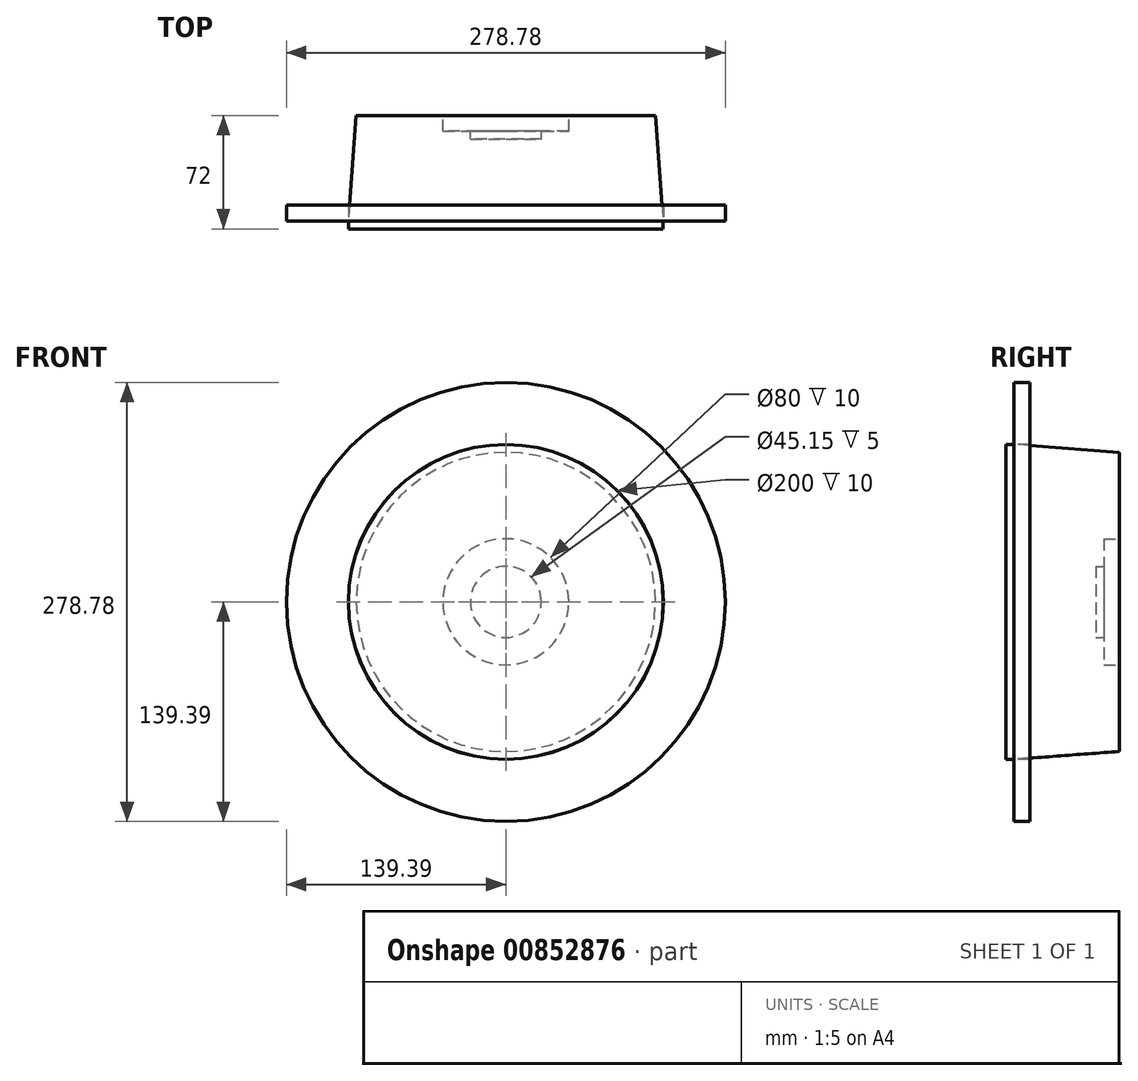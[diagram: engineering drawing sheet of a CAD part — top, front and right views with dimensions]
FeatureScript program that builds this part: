
annotation { "Feature Type Name" : "Feature", "Feature Type Description" : "" }
export const myFeature = defineFeature(function(context is Context, id is Id, definition is map)
    precondition{}
    {
        {
            var Q0;
            Q0=qCreatedBy(makeId("Front.planeOp"),FACE);
            var sketch = newSketch(context, id + "F0", { "sketchPlane" : qUnion([Q0])});
            skCircle(sketch, "E0", {"center": v(0, 0) * mm, "radius": 100 * mm});
            skLineSegment(sketch, "E1.bottom", {"start": v(90.04, 43.5) * mm, "end": v(90.04, 43.5) * mm});
            skLineSegment(sketch, "E1.top", {"start": v(90.04, -43.5) * mm, "end": v(90.04, -43.5) * mm});
            skCircle(sketch, "E2", {"center": v(0, 0) * mm, "radius": 139.39 * mm});
            skCircle(sketch, "E3", {"center": v(0, 0) * mm, "radius": 99.95 * mm});
            skSolve(sketch);
        }
        {
            var Q0;
            Q0=makeQuery(id+"F0.imprint","IMPRINT",FACE,{"disambiguationData":[TD([[makeQuery(id+"F0.imprint","IMPRINT",EDGE,{"derivedFrom":sQuery(id+"F0.wireOp",EDGE,"E2")}),1.0]])]});
            extrude(context, id + "F1", {"entities" : qUnion([Q0]), "oppositeDirection" : true, "depth" : 10 * mm, "offsetDistance" : 25 * mm});
        }
        {
            var Q0;
            {var subQ1=sQuery(id+"F0.wireOp",EDGE,"O6Og0VBV-7w1m-iwyO-GZB4-oZ87gUU7icq7");Q0=makeQuery(id+"F0.imprint","IMPRINT",FACE,{"disambiguationData":[TD([[makeQuery(id+"F0.imprint","IMPRINT",EDGE,{"derivedFrom":subQ1}),-1.0]])]});}
            var Q1;
            {var subQ0=sQuery(id+"F0.wireOp",EDGE,"E1.right");Q1=makeQuery(id+"F0.imprint","IMPRINT",FACE,{"disambiguationData":[TD([[makeQuery(id+"F0.imprint","IMPRINT",EDGE,{"derivedFrom":subQ0}),1.0]])]});}
            var Q2;
            Q2=makeQuery(id+"F0.imprint","IMPRINT",FACE,{"disambiguationData":[TD([[makeQuery(id+"F0.imprint","IMPRINT",EDGE,{"derivedFrom":sQuery(id+"F0.wireOp",EDGE,"O6Og0VBV-7w1m-iwyO-GZB4-oZ87gUU7icq7")}),1.0]])]});
            var Q3;
            Q3=makeQuery(id+"F0.imprint","IMPRINT",FACE,{"disambiguationData":[TD([[makeQuery(id+"F0.imprint","IMPRINT",EDGE,{"derivedFrom":sQuery(id+"F0.wireOp",EDGE,"GIwreYSu-AWBa-Gf9F-D9ee-HEHceEFpZMHu")}),-1.0]])]});
            var Q4;
            Q4=makeQuery(id+"F0.imprint","IMPRINT",FACE,{"disambiguationData":[TD([[makeQuery(id+"F0.imprint","IMPRINT",EDGE,{"derivedFrom":sQuery(id+"F0.wireOp",EDGE,"E2")}),1.0]])]});
            var Q5;
            {var subQ0=sQuery(id+"F0.wireOp",EDGE,"iStEkPqN-RXga-rDrQ-Osgs-Vn1kGgOUYUa5");Q5=makeQuery(id+"F0.imprint","IMPRINT",FACE,{"disambiguationData":[TD([[makeQuery(id+"F0.imprint","IMPRINT",EDGE,{"derivedFrom":subQ0}),-1.0]])]});}
            extrude(context, id + "F2", {"entities" : qUnion([Q0, Q1, Q2, Q3, Q4, Q5]), "oppositeDirection" : true, "depth" : 10 * mm, "offsetDistance" : 25 * mm});
        }
        {
            var Q0;
            {var subQ0=sQuery(id+"F0.wireOp",EDGE,"E3");Q0=makeQuery(id+"F3zxJdrnI9NYqlr_0.boolean.opBoolean","MERGE",FACE,{"derivedFrom":[makeQuery(id+"F2.opExtrude","CAP_FACE",FACE,{"disambiguationData":[OSD([sQuery(id+"F0.wireOp",EDGE,"E0"),sQuery(id+"F0.wireOp",EDGE,"E1.right"),sQuery(id+"F0.wireOp",EDGE,"GIwreYSu-AWBa-Gf9F-D9ee-HEHceEFpZMHu"),sQuery(id+"F0.wireOp",EDGE,"1ppw7uot-TYSR-niU3-FFL4-BmLDpTlKCJTZ"),sQuery(id+"F0.wireOp",EDGE,"iStEkPqN-RXga-rDrQ-Osgs-Vn1kGgOUYUa5"),sQuery(id+"F0.wireOp",EDGE,"E2"),subQ0])],"isStart":true}),makeQuery(id+"F3zxJdrnI9NYqlr_0.opExtrude","CAP_FACE",FACE,{"disambiguationData":[OSD([subQ0])],"isStart":true})]});}
            var sketch = newSketch(context, id + "F3", { "sketchPlane" : qUnion([Q0])});
            skCircle(sketch, "E4", {"center": v(0, 0) * mm, "radius": 100 * mm});
            skSolve(sketch);
        }
        {
            var Q0;
            Q0=makeQuery(id+"F0.imprint","IMPRINT",FACE,{"disambiguationData":[TD([[makeQuery(id+"F0.imprint","IMPRINT",EDGE,{"derivedFrom":sQuery(id+"F0.wireOp",EDGE,"E3")}),1.0]])]});
            extrude(context, id + "F4", {"entities" : qUnion([Q0]), "depth" : 5 * mm, "offsetDistance" : 25 * mm});
        }
        {
            var Q0;
            Q0=makeQuery(id+"F1.opExtrude","CAP_FACE",FACE,{"disambiguationData":[OSD([sQuery(id+"F0.wireOp",EDGE,"E0"),sQuery(id+"F0.wireOp",EDGE,"E2")])],"isStart":false});
            cPlane(context, id + "F5", {"entities" : qUnion([Q0]), "cplaneType" : CPlaneType.OFFSET, "offset" : 57 * mm, "width" : 150 * mm, "height" : 150 * mm});
        }
        {
            var Q0;
            Q0=qCreatedBy(id+"F5.planeOp",FACE);
            var sketch = newSketch(context, id + "F6", { "sketchPlane" : qUnion([Q0])});
            skCircle(sketch, "E5", {"center": v(0, 0) * mm, "radius": 95 * mm});
            skSolve(sketch);
        }
        {
            var Q1;
            Q1 = qSketchRegion(id + "F3", true);
            var Q2;
            Q2 = qSketchRegion(id + "F6", true);
            loft(context, id + "F7", {"operationType" : NewBodyOperationType.ADD, "sheetProfilesArray" : [{ "sheetProfileEntities" : qUnion([Q1]) }, { "sheetProfileEntities" : qUnion([Q2]) }]});
        }
        {
            var Q0;
            Q0=qCreatedBy(id+"F5.planeOp",FACE);
            var sketch = newSketch(context, id + "F8", { "sketchPlane" : qUnion([Q0])});
            skCircle(sketch, "E6", {"center": v(0, 0) * mm, "radius": 40 * mm});
            skSolve(sketch);
        }
        {
            var Q0;
            Q0 = qSketchRegion(id + "F8", true);
            extrude(context, id + "F9", {"entities" : qUnion([Q0]), "operationType" : NewBodyOperationType.REMOVE, "oppositeDirection" : true, "depth" : 10 * mm, "offsetDistance" : 25 * mm});
        }
        {
            var Q0;
            Q0=makeQuery(id+"F9.boolean.opBoolean","COPY",FACE,{"derivedFrom":makeQuery(id+"F9.opExtrude","CAP_FACE",FACE,{"disambiguationData":[OSD([sQuery(id+"F8.wireOp",EDGE,"E6")])],"isStart":false})});
            var sketch = newSketch(context, id + "F10", { "sketchPlane" : qUnion([Q0])});
            skCircle(sketch, "E7", {"center": v(0, 0) * mm, "radius": 22.58 * mm});
            skSolve(sketch);
        }
        {
            var Q0;
            Q0=makeQuery(id+"F10.imprint","IMPRINT",FACE,{"disambiguationData":[TD([[makeQuery(id+"F10.imprint","IMPRINT",EDGE,{"derivedFrom":sQuery(id+"F10.wireOp",EDGE,"E7")}),1.0]])]});
            extrude(context, id + "F11", {"entities" : qUnion([Q0]), "operationType" : NewBodyOperationType.REMOVE, "oppositeDirection" : true, "depth" : 5 * mm, "offsetDistance" : 25 * mm});
        }
    });
